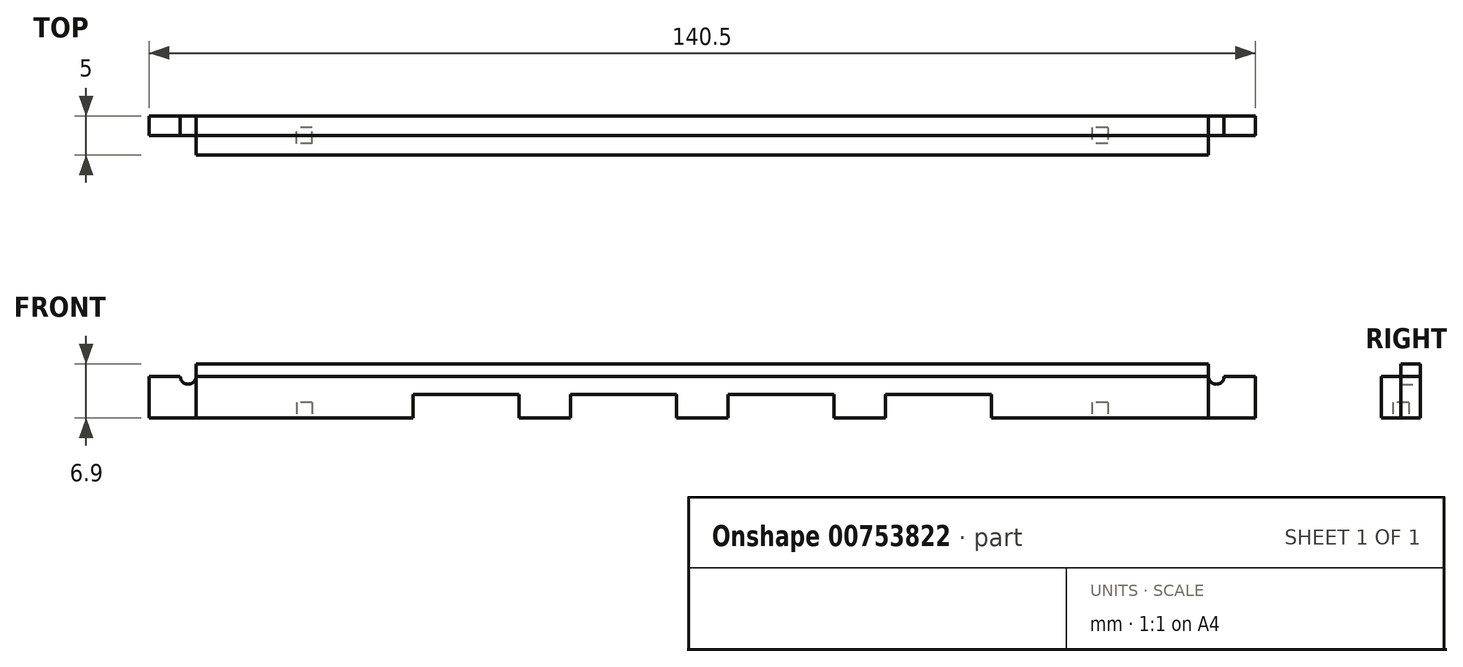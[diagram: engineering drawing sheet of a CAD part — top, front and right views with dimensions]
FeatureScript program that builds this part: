
annotation { "Feature Type Name" : "Feature", "Feature Type Description" : "" }
export const myFeature = defineFeature(function(context is Context, id is Id, definition is map)
    precondition{}
    {
        {
            var Q0;
            Q0=qCreatedBy(makeId("Front.planeOp"),FACE);
            var sketch = newSketch(context, id + "F0", { "sketchPlane" : qUnion([Q0])});
            skLineSegment(sketch, "E0.bottom", {"start": v(64.3, 7.08) * mm, "end": v(-64.3, 7.08) * mm});
            skLineSegment(sketch, "E0.left", {"start": v(64.3, 7.08) * mm, "end": v(64.3, -6.72) * mm});
            skLineSegment(sketch, "E0.right", {"start": v(-64.3, 7.08) * mm, "end": v(-64.3, -6.72) * mm});
            skPoint(sketch, "E0.middle", {"position": v(0, 0.18) * mm});
            skLineSegment(sketch, "E1.top", {"start": v(-70.25, 5.48) * mm, "end": v(70.25, 5.48) * mm});
            skLineSegment(sketch, "E1.left", {"start": v(-70.25, -6.72) * mm, "end": v(-70.25, 5.48) * mm});
            skLineSegment(sketch, "E1.right", {"start": v(70.25, -6.72) * mm, "end": v(70.25, 5.48) * mm});
            skCircle(sketch, "E2", {"center": v(65.3, 5.48) * mm, "radius": 1 * mm});
            skCircle(sketch, "E3", {"center": v(-65.3, 5.48) * mm, "radius": 1 * mm});
            skLineSegment(sketch, "E4.bottom", {"start": v(-23.25, 3.18) * mm, "end": v(-36.75, 3.18) * mm});
            skLineSegment(sketch, "E4.left", {"start": v(-23.25, 3.18) * mm, "end": v(-23.25, -2.82) * mm});
            skLineSegment(sketch, "E4.right", {"start": v(-36.75, 3.18) * mm, "end": v(-36.75, -2.82) * mm});
            skPoint(sketch, "E4.middle", {"position": v(-30, 0.18) * mm});
            skLineSegment(sketch, "E5.bottom", {"start": v(-3.25, 3.18) * mm, "end": v(-16.75, 3.18) * mm});
            skLineSegment(sketch, "E5.left", {"start": v(-3.25, 3.18) * mm, "end": v(-3.25, -2.82) * mm});
            skLineSegment(sketch, "E5.right", {"start": v(-16.75, 3.18) * mm, "end": v(-16.75, -2.82) * mm});
            skPoint(sketch, "E5.middle", {"position": v(-10, 0.18) * mm});
            skLineSegment(sketch, "E6.bottom", {"start": v(16.75, 3.18) * mm, "end": v(3.25, 3.18) * mm});
            skLineSegment(sketch, "E6.left", {"start": v(16.75, 3.18) * mm, "end": v(16.75, -2.82) * mm});
            skLineSegment(sketch, "E6.right", {"start": v(3.25, 3.18) * mm, "end": v(3.25, -2.82) * mm});
            skPoint(sketch, "E6.middle", {"position": v(10, 0.18) * mm});
            skLineSegment(sketch, "E7.bottom", {"start": v(36.75, 3.18) * mm, "end": v(23.25, 3.18) * mm});
            skLineSegment(sketch, "E7.left", {"start": v(36.75, 3.18) * mm, "end": v(36.75, -2.82) * mm});
            skLineSegment(sketch, "E7.right", {"start": v(23.25, 3.18) * mm, "end": v(23.25, -2.82) * mm});
            skPoint(sketch, "E7.middle", {"position": v(30, 0.18) * mm});
            skPoint(sketch, "E8", {"position": v(-36.75, 0.18) * mm});
            skPoint(sketch, "E9", {"position": v(36.75, 0.18) * mm});
            skPoint(sketch, "E10", {"position": v(-70.25, 0.18) * mm});
            skPoint(sketch, "E11", {"position": v(70.25, 0.18) * mm});
            skLineSegment(sketch, "E12", {"start": v(-70.25, 0.18) * mm, "end": v(70.25, 0.18) * mm});
            skSolve(sketch);
        }
        {
            var Q0;
            {var subQ8=sQuery(id+"F0.wireOp",EDGE,"E4.bottom");Q0=makeQuery(id+"F0.imprint","IMPRINT",FACE,{"disambiguationData":[TD([[makeQuery(id+"F0.imprint","IMPRINT",EDGE,{"derivedFrom":subQ8}),-1.0]])]});}
            extrude(context, id + "F1", {"entities" : qUnion([Q0]), "depth" : 5 * mm, "offsetDistance" : 25 * mm});
        }
        {
            var Q0;
            {var subQ1=sQuery(id+"F0.wireOp",EDGE,"E1.top");var subQ7=sQuery(id+"F0.wireOp",EDGE,"E1.left");var subQ8=makeQuery(id+"F0.imprint","INTERSECT",VERTEX,{"derivedFrom":[subQ1,subQ7]});Q0=makeQuery(id+"F0.imprint","IMPRINT",FACE,{"disambiguationData":[TD([[makeQuery(id+"F0.imprint","IMPRINT",EDGE,{"disambiguationData":[TD([[subQ8,-1.0]])],"derivedFrom":subQ1}),-1.0]])]});}
            var Q1;
            {var subQ0=sQuery(id+"F0.wireOp",EDGE,"E0.bottom");Q1=makeQuery(id+"F0.imprint","IMPRINT",FACE,{"disambiguationData":[TD([[makeQuery(id+"F0.imprint","IMPRINT",EDGE,{"derivedFrom":subQ0}),1.0]])]});}
            var Q2;
            {var subQ1=sQuery(id+"F0.wireOp",EDGE,"E1.top");var subQ7=sQuery(id+"F0.wireOp",EDGE,"E1.right");var subQ8=makeQuery(id+"F0.imprint","INTERSECT",VERTEX,{"derivedFrom":[subQ1,subQ7]});Q2=makeQuery(id+"F0.imprint","IMPRINT",FACE,{"disambiguationData":[TD([[makeQuery(id+"F0.imprint","IMPRINT",EDGE,{"disambiguationData":[TD([[subQ8,1.0]])],"derivedFrom":subQ1}),-1.0]])]});}
            extrude(context, id + "F2", {"entities" : qUnion([Q0, Q1, Q2]), "operationType" : NewBodyOperationType.ADD, "depth" : 2.5 * mm, "offsetDistance" : 25 * mm});
        }
        {
            var Q0;
            {var subQ0=sQuery(id+"F0.wireOp",EDGE,"E12");var subQ1=makeQuery(id+"F0.imprint","INTERSECT",VERTEX,{"derivedFrom":[sQuery(id+"F0.wireOp",EDGE,"E0.left"),subQ0]});Q0=makeQuery(id+"F2.boolean.opBoolean","MERGE",FACE,{"derivedFrom":[makeQuery(id+"F1.opExtrude","SWEPT_FACE",FACE,{"disambiguationData":[OSD([subQ0]),TDD([makeQuery(id+"F0.imprint","IMPRINT",EDGE,{"disambiguationData":[TD([[subQ1,1.0]])],"derivedFrom":subQ0})])]}),makeQuery(id+"F2.opExtrude","SWEPT_FACE",FACE,{"disambiguationData":[OSD([subQ0]),TDD([makeQuery(id+"F0.imprint","IMPRINT",EDGE,{"disambiguationData":[TD([[makeQuery(id+"F0.imprint","INTERSECT",VERTEX,{"derivedFrom":[sQuery(id+"F0.wireOp",EDGE,"E1.right"),subQ0]}),1.0]])],"derivedFrom":subQ0})])]})]});}
            var sketch = newSketch(context, id + "F3", { "sketchPlane" : qUnion([Q0])});
            skLineSegment(sketch, "E13", {"start": v(50.52, 5) * mm, "end": v(50.52, 0) * mm, "construction": true});
            skPoint(sketch, "E14", {"position": v(50.52, 2.5) * mm});
            skLineSegment(sketch, "E15.bottom", {"start": v(51.52, 1.5) * mm, "end": v(49.52, 1.5) * mm});
            skLineSegment(sketch, "E15.top", {"start": v(51.52, 3.5) * mm, "end": v(49.52, 3.5) * mm});
            skLineSegment(sketch, "E15.left", {"start": v(51.52, 1.5) * mm, "end": v(51.52, 3.5) * mm});
            skLineSegment(sketch, "E15.right", {"start": v(49.52, 1.5) * mm, "end": v(49.52, 3.5) * mm});
            skSolve(sketch);
        }
        {
            var Q0;
            Q0=makeQuery(id+"F3.imprint","IMPRINT",FACE,{"disambiguationData":[TD([[makeQuery(id+"F3.imprint","IMPRINT",EDGE,{"derivedFrom":sQuery(id+"F3.wireOp",EDGE,"E15.bottom")}),-1.0]])]});
            extrude(context, id + "F4", {"entities" : qUnion([Q0]), "operationType" : NewBodyOperationType.REMOVE, "oppositeDirection" : true, "depth" : 2 * mm, "offsetDistance" : 25 * mm});
        }
        {
            var Q0;
            {var subQ0=sQuery(id+"F0.wireOp",EDGE,"E12");var subQ1=makeQuery(id+"F0.imprint","INTERSECT",VERTEX,{"derivedFrom":[sQuery(id+"F0.wireOp",EDGE,"E0.right"),subQ0]});Q0=makeQuery(id+"F2.boolean.opBoolean","MERGE",FACE,{"derivedFrom":[makeQuery(id+"F1.opExtrude","SWEPT_FACE",FACE,{"disambiguationData":[OSD([subQ0]),TDD([makeQuery(id+"F0.imprint","IMPRINT",EDGE,{"disambiguationData":[TD([[subQ1,-1.0]])],"derivedFrom":subQ0})])]}),makeQuery(id+"F2.opExtrude","SWEPT_FACE",FACE,{"disambiguationData":[OSD([subQ0]),TDD([makeQuery(id+"F0.imprint","IMPRINT",EDGE,{"disambiguationData":[TD([[makeQuery(id+"F0.imprint","INTERSECT",VERTEX,{"derivedFrom":[sQuery(id+"F0.wireOp",EDGE,"E1.left"),subQ0]}),-1.0]])],"derivedFrom":subQ0})])]})]});}
            var sketch = newSketch(context, id + "F5", { "sketchPlane" : qUnion([Q0])});
            skLineSegment(sketch, "E16", {"start": v(-50.52, 5) * mm, "end": v(-50.52, 0) * mm, "construction": true});
            skPoint(sketch, "E17", {"position": v(-50.52, 2.5) * mm});
            skLineSegment(sketch, "E18.bottom", {"start": v(-49.52, 3.5) * mm, "end": v(-51.52, 3.5) * mm});
            skLineSegment(sketch, "E18.top", {"start": v(-49.52, 1.5) * mm, "end": v(-51.52, 1.5) * mm});
            skLineSegment(sketch, "E18.left", {"start": v(-49.52, 3.5) * mm, "end": v(-49.52, 1.5) * mm});
            skLineSegment(sketch, "E18.right", {"start": v(-51.52, 3.5) * mm, "end": v(-51.52, 1.5) * mm});
            skSolve(sketch);
        }
        {
            var Q0;
            Q0=makeQuery(id+"F5.imprint","IMPRINT",FACE,{"disambiguationData":[TD([[makeQuery(id+"F5.imprint","IMPRINT",EDGE,{"derivedFrom":sQuery(id+"F5.wireOp",EDGE,"E18.bottom")}),1.0]])]});
            extrude(context, id + "F6", {"entities" : qUnion([Q0]), "operationType" : NewBodyOperationType.REMOVE, "oppositeDirection" : true, "depth" : 2 * mm, "offsetDistance" : 25 * mm});
        }
    });
